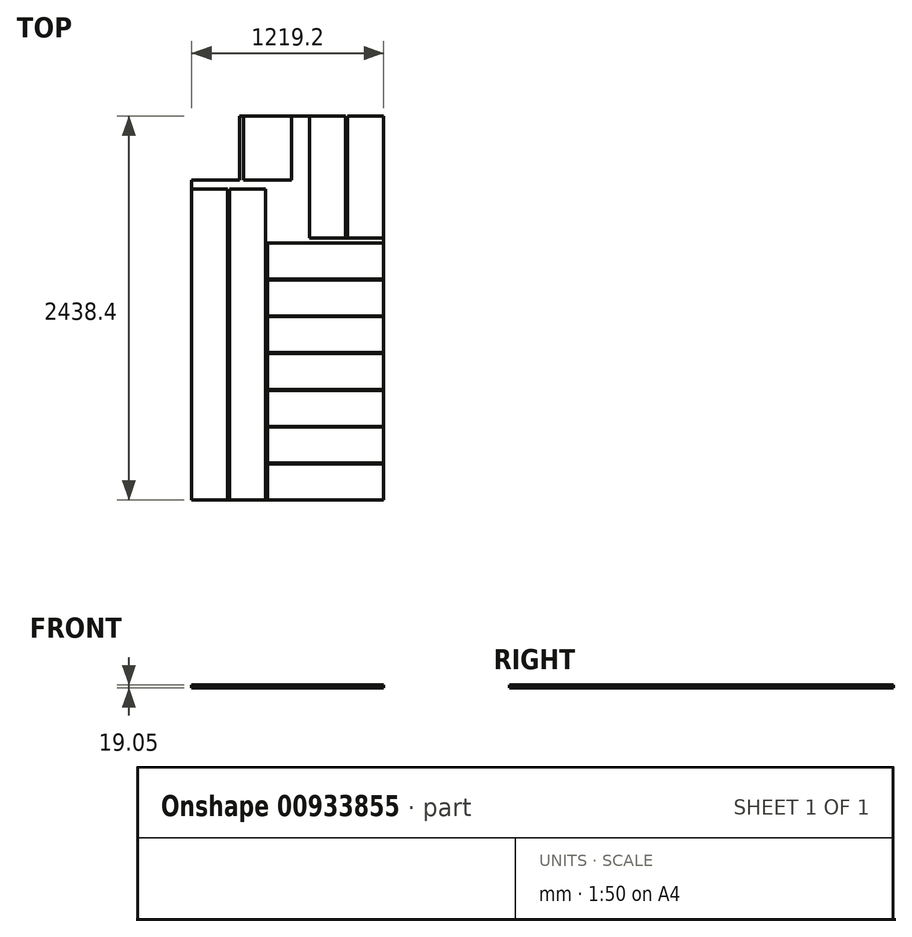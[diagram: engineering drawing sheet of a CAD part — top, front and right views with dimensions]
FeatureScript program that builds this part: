
annotation { "Feature Type Name" : "Feature", "Feature Type Description" : "" }
export const myFeature = defineFeature(function(context is Context, id is Id, definition is map)
    precondition{}
    {
        {
            var Q0;
            Q0=qCreatedBy(makeId("Top.planeOp"),FACE);
            var sketch = newSketch(context, id + "F0", { "sketchPlane" : qUnion([Q0])});
            skLineSegment(sketch, "E0.bottom", {"start": v(0, 0) * mm, "end": v(1219.2, 0) * mm, "construction": true});
            skLineSegment(sketch, "E0.top", {"start": v(0, 2438.4) * mm, "end": v(1219.2, 2438.4) * mm, "construction": true});
            skLineSegment(sketch, "E0.left", {"start": v(0, 0) * mm, "end": v(0, 2438.4) * mm, "construction": true});
            skLineSegment(sketch, "E0.right", {"start": v(1219.2, 0) * mm, "end": v(1219.2, 2438.4) * mm, "construction": true});
            skLineSegment(sketch, "E1.bottom", {"start": v(0, 0) * mm, "end": v(228.6, 0) * mm});
            skLineSegment(sketch, "E1.top", {"start": v(0, 1974.85) * mm, "end": v(228.6, 1974.85) * mm});
            skLineSegment(sketch, "E1.left", {"start": v(0, 0) * mm, "end": v(0, 1974.85) * mm});
            skLineSegment(sketch, "E1.right", {"start": v(228.6, 0) * mm, "end": v(228.6, 1974.85) * mm});
            skLineSegment(sketch, "E2.bottom", {"start": v(241.3, 0) * mm, "end": v(469.9, 0) * mm});
            skLineSegment(sketch, "E2.top", {"start": v(241.3, 1974.85) * mm, "end": v(469.9, 1974.85) * mm});
            skLineSegment(sketch, "E2.left", {"start": v(241.3, 0) * mm, "end": v(241.3, 1974.85) * mm});
            skLineSegment(sketch, "E2.right", {"start": v(469.9, 0) * mm, "end": v(469.9, 1974.85) * mm});
            skLineSegment(sketch, "E3.bottom", {"start": v(1219.2, 0) * mm, "end": v(482.6, 0) * mm});
            skLineSegment(sketch, "E3.top", {"start": v(1219.2, 228.6) * mm, "end": v(482.6, 228.6) * mm});
            skLineSegment(sketch, "E3.left", {"start": v(1219.2, 0) * mm, "end": v(1219.2, 228.6) * mm});
            skLineSegment(sketch, "E3.right", {"start": v(482.6, 0) * mm, "end": v(482.6, 228.6) * mm});
            skLineSegment(sketch, "E4.bottom", {"start": v(1219.2, 233.68) * mm, "end": v(482.6, 233.68) * mm});
            skLineSegment(sketch, "E4.top", {"start": v(1219.2, 462.28) * mm, "end": v(482.6, 462.28) * mm});
            skLineSegment(sketch, "E4.left", {"start": v(1219.2, 233.68) * mm, "end": v(1219.2, 462.28) * mm});
            skLineSegment(sketch, "E4.right", {"start": v(482.6, 233.68) * mm, "end": v(482.6, 462.28) * mm});
            skLineSegment(sketch, "E5.bottom", {"start": v(1219.2, 467.36) * mm, "end": v(482.6, 467.36) * mm});
            skLineSegment(sketch, "E5.top", {"start": v(1219.2, 695.96) * mm, "end": v(482.6, 695.96) * mm});
            skLineSegment(sketch, "E5.left", {"start": v(1219.2, 467.36) * mm, "end": v(1219.2, 695.96) * mm});
            skLineSegment(sketch, "E5.right", {"start": v(482.6, 467.36) * mm, "end": v(482.6, 695.96) * mm});
            skLineSegment(sketch, "E6.bottom", {"start": v(1219.2, 701.04) * mm, "end": v(482.6, 701.04) * mm});
            skLineSegment(sketch, "E6.top", {"start": v(1219.2, 929.64) * mm, "end": v(482.6, 929.64) * mm});
            skLineSegment(sketch, "E6.left", {"start": v(1219.2, 701.04) * mm, "end": v(1219.2, 929.64) * mm});
            skLineSegment(sketch, "E6.right", {"start": v(482.6, 701.04) * mm, "end": v(482.6, 929.64) * mm});
            skLineSegment(sketch, "E7.bottom", {"start": v(1219.2, 934.72) * mm, "end": v(482.6, 934.72) * mm});
            skLineSegment(sketch, "E7.top", {"start": v(1219.2, 1163.32) * mm, "end": v(482.6, 1163.32) * mm});
            skLineSegment(sketch, "E7.left", {"start": v(1219.2, 934.72) * mm, "end": v(1219.2, 1163.32) * mm});
            skLineSegment(sketch, "E7.right", {"start": v(482.6, 934.72) * mm, "end": v(482.6, 1163.32) * mm});
            skLineSegment(sketch, "E8.bottom", {"start": v(1219.2, 1168.4) * mm, "end": v(482.6, 1168.4) * mm});
            skLineSegment(sketch, "E8.top", {"start": v(1219.2, 1397) * mm, "end": v(482.6, 1397) * mm});
            skLineSegment(sketch, "E8.left", {"start": v(1219.2, 1168.4) * mm, "end": v(1219.2, 1397) * mm});
            skLineSegment(sketch, "E8.right", {"start": v(482.6, 1168.4) * mm, "end": v(482.6, 1397) * mm});
            skLineSegment(sketch, "E9.bottom", {"start": v(1219.2, 1402.08) * mm, "end": v(482.6, 1402.08) * mm});
            skLineSegment(sketch, "E9.top", {"start": v(1219.2, 1630.68) * mm, "end": v(482.6, 1630.68) * mm});
            skLineSegment(sketch, "E9.left", {"start": v(1219.2, 1402.08) * mm, "end": v(1219.2, 1630.68) * mm});
            skLineSegment(sketch, "E9.right", {"start": v(482.6, 1402.08) * mm, "end": v(482.6, 1630.68) * mm});
            skLineSegment(sketch, "E10.bottom", {"start": v(1219.2, 2438.4) * mm, "end": v(990.6, 2438.4) * mm});
            skLineSegment(sketch, "E10.top", {"start": v(1219.2, 1663.7) * mm, "end": v(990.6, 1663.7) * mm});
            skLineSegment(sketch, "E10.left", {"start": v(1219.2, 2438.4) * mm, "end": v(1219.2, 1663.7) * mm});
            skLineSegment(sketch, "E10.right", {"start": v(990.6, 2438.4) * mm, "end": v(990.6, 1663.7) * mm});
            skLineSegment(sketch, "E11.bottom", {"start": v(977.9, 2438.4) * mm, "end": v(749.3, 2438.4) * mm});
            skLineSegment(sketch, "E11.top", {"start": v(977.9, 1663.7) * mm, "end": v(749.3, 1663.7) * mm});
            skLineSegment(sketch, "E11.left", {"start": v(977.9, 2438.4) * mm, "end": v(977.9, 1663.7) * mm});
            skLineSegment(sketch, "E11.right", {"start": v(749.3, 2438.4) * mm, "end": v(749.3, 1663.7) * mm});
            skLineSegment(sketch, "E12", {"start": v(749.3, 2438.4) * mm, "end": v(0, 2438.4) * mm});
            skLineSegment(sketch, "E13", {"start": v(0, 1974.85) * mm, "end": v(469.9, 1974.85) * mm});
            skLineSegment(sketch, "E14", {"start": v(0, 2438.4) * mm, "end": v(0, 1974.85) * mm});
            skLineSegment(sketch, "E15", {"start": v(228.6, 1974.85) * mm, "end": v(228.6, 0) * mm});
            skLineSegment(sketch, "E16", {"start": v(228.6, 0) * mm, "end": v(241.3, 0) * mm});
            skLineSegment(sketch, "E17", {"start": v(241.3, 1974.85) * mm, "end": v(241.3, 0) * mm});
            skLineSegment(sketch, "E18", {"start": v(469.9, 1974.85) * mm, "end": v(469.9, 0) * mm});
            skLineSegment(sketch, "E19", {"start": v(469.9, 0) * mm, "end": v(482.6, 0) * mm});
            skLineSegment(sketch, "E20", {"start": v(482.6, 0) * mm, "end": v(482.6, 1630.68) * mm});
            skLineSegment(sketch, "E21", {"start": v(482.6, 1630.68) * mm, "end": v(1219.2, 1630.68) * mm});
            skLineSegment(sketch, "E22", {"start": v(1219.2, 1630.68) * mm, "end": v(1219.2, 1663.7) * mm});
            skLineSegment(sketch, "E23", {"start": v(990.6, 1663.7) * mm, "end": v(990.6, 2438.4) * mm});
            skLineSegment(sketch, "E24", {"start": v(990.6, 2438.4) * mm, "end": v(977.9, 2438.4) * mm});
            skLineSegment(sketch, "E25", {"start": v(990.6, 1663.7) * mm, "end": v(749.3, 1663.7) * mm});
            skLineSegment(sketch, "E26", {"start": v(749.3, 1663.7) * mm, "end": v(749.3, 2438.4) * mm});
            skLineSegment(sketch, "E27", {"start": v(990.6, 1663.7) * mm, "end": v(977.9, 1663.7) * mm});
            skLineSegment(sketch, "E28", {"start": v(1219.2, 228.6) * mm, "end": v(1219.2, 233.68) * mm});
            skLineSegment(sketch, "E29", {"start": v(1219.2, 462.28) * mm, "end": v(1219.2, 467.36) * mm});
            skLineSegment(sketch, "E30", {"start": v(1219.2, 695.96) * mm, "end": v(1219.2, 701.04) * mm});
            skLineSegment(sketch, "E31", {"start": v(1219.2, 929.64) * mm, "end": v(1219.2, 934.72) * mm});
            skLineSegment(sketch, "E32", {"start": v(1219.2, 1163.32) * mm, "end": v(1219.2, 1168.4) * mm});
            skLineSegment(sketch, "E33", {"start": v(1219.2, 1402.08) * mm, "end": v(1219.2, 1397) * mm});
            skLineSegment(sketch, "E34.bottom", {"start": v(0, 2438.4) * mm, "end": v(304.8, 2438.4) * mm});
            skLineSegment(sketch, "E34.top", {"start": v(0, 2032) * mm, "end": v(304.8, 2032) * mm});
            skLineSegment(sketch, "E34.left", {"start": v(0, 2438.4) * mm, "end": v(0, 2032) * mm});
            skLineSegment(sketch, "E34.right", {"start": v(304.8, 2438.4) * mm, "end": v(304.8, 2032) * mm});
            skLineSegment(sketch, "E35.bottom", {"start": v(374.65, 2438.4) * mm, "end": v(679.45, 2438.4) * mm});
            skLineSegment(sketch, "E36.bottom", {"start": v(330.2, 2438.4) * mm, "end": v(635, 2438.4) * mm});
            skLineSegment(sketch, "E36.top", {"start": v(330.2, 2032) * mm, "end": v(635, 2032) * mm});
            skLineSegment(sketch, "E36.left", {"start": v(330.2, 2438.4) * mm, "end": v(330.2, 2032) * mm});
            skLineSegment(sketch, "E36.right", {"start": v(635, 2438.4) * mm, "end": v(635, 2032) * mm});
            skSolve(sketch);
        }
        {
            var Q0;
            Q0=makeQuery(id+"F0.imprint","IMPRINT",FACE,{"disambiguationData":[TD([[makeQuery(id+"F0.imprint","IMPRINT",EDGE,{"derivedFrom":sQuery(id+"F0.wireOp",EDGE,"E12")}),1.0]])]});
            var Q1;
            Q1=makeQuery(id+"F0.imprint","IMPRINT",FACE,{"disambiguationData":[TD([[makeQuery(id+"F0.imprint","IMPRINT",EDGE,{"derivedFrom":sQuery(id+"F0.wireOp",EDGE,"E13")}),-1.0]])]});
            var Q2;
            Q2=makeQuery(id+"F0.imprint","IMPRINT",FACE,{"disambiguationData":[TD([[makeQuery(id+"F0.imprint","IMPRINT",EDGE,{"derivedFrom":sQuery(id+"F0.wireOp",EDGE,"E23")}),1.0]])]});
            var Q3;
            {var subQ0=sQuery(id+"F0.wireOp",EDGE,"E8.top");Q3=makeQuery(id+"F0.imprint","IMPRINT",FACE,{"disambiguationData":[TD([[makeQuery(id+"F0.imprint","IMPRINT",EDGE,{"derivedFrom":subQ0}),-1.0]])]});}
            var Q4;
            {var subQ0=sQuery(id+"F0.wireOp",EDGE,"E7.top");Q4=makeQuery(id+"F0.imprint","IMPRINT",FACE,{"disambiguationData":[TD([[makeQuery(id+"F0.imprint","IMPRINT",EDGE,{"derivedFrom":subQ0}),-1.0]])]});}
            var Q5;
            {var subQ0=sQuery(id+"F0.wireOp",EDGE,"E6.top");Q5=makeQuery(id+"F0.imprint","IMPRINT",FACE,{"disambiguationData":[TD([[makeQuery(id+"F0.imprint","IMPRINT",EDGE,{"derivedFrom":subQ0}),-1.0]])]});}
            var Q6;
            {var subQ0=sQuery(id+"F0.wireOp",EDGE,"E5.top");Q6=makeQuery(id+"F0.imprint","IMPRINT",FACE,{"disambiguationData":[TD([[makeQuery(id+"F0.imprint","IMPRINT",EDGE,{"derivedFrom":subQ0}),-1.0]])]});}
            var Q7;
            {var subQ0=sQuery(id+"F0.wireOp",EDGE,"E4.top");Q7=makeQuery(id+"F0.imprint","IMPRINT",FACE,{"disambiguationData":[TD([[makeQuery(id+"F0.imprint","IMPRINT",EDGE,{"derivedFrom":subQ0}),-1.0]])]});}
            var Q8;
            {var subQ0=sQuery(id+"F0.wireOp",EDGE,"E3.top");Q8=makeQuery(id+"F0.imprint","IMPRINT",FACE,{"disambiguationData":[TD([[makeQuery(id+"F0.imprint","IMPRINT",EDGE,{"derivedFrom":subQ0}),-1.0]])]});}
            extrude(context, id + "F1", {"entities" : qUnion([Q0, Q1, Q2, Q3, Q4, Q5, Q6, Q7, Q8]), "depth" : 19.05 * mm, "offsetDistance" : 25.4 * mm});
        }
        {
            var Q0;
            Q0=makeQuery(id+"F0.imprint","IMPRINT",FACE,{"disambiguationData":[TD([[makeQuery(id+"F0.imprint","IMPRINT",EDGE,{"derivedFrom":sQuery(id+"F0.wireOp",EDGE,"E1.bottom")}),1.0]])]});
            var Q1;
            Q1=makeQuery(id+"F0.imprint","IMPRINT",FACE,{"disambiguationData":[TD([[makeQuery(id+"F0.imprint","IMPRINT",EDGE,{"derivedFrom":sQuery(id+"F0.wireOp",EDGE,"E2.bottom")}),1.0]])]});
            var Q2;
            {var subQ0=sQuery(id+"F0.wireOp",EDGE,"E9.bottom");Q2=makeQuery(id+"F0.imprint","IMPRINT",FACE,{"disambiguationData":[TD([[makeQuery(id+"F0.imprint","IMPRINT",EDGE,{"derivedFrom":subQ0}),-1.0]])]});}
            var Q3;
            {var subQ0=sQuery(id+"F0.wireOp",EDGE,"E8.bottom");Q3=makeQuery(id+"F0.imprint","IMPRINT",FACE,{"disambiguationData":[TD([[makeQuery(id+"F0.imprint","IMPRINT",EDGE,{"derivedFrom":subQ0}),-1.0]])]});}
            var Q4;
            {var subQ0=sQuery(id+"F0.wireOp",EDGE,"E7.bottom");Q4=makeQuery(id+"F0.imprint","IMPRINT",FACE,{"disambiguationData":[TD([[makeQuery(id+"F0.imprint","IMPRINT",EDGE,{"derivedFrom":subQ0}),-1.0]])]});}
            var Q5;
            {var subQ0=sQuery(id+"F0.wireOp",EDGE,"E6.bottom");Q5=makeQuery(id+"F0.imprint","IMPRINT",FACE,{"disambiguationData":[TD([[makeQuery(id+"F0.imprint","IMPRINT",EDGE,{"derivedFrom":subQ0}),-1.0]])]});}
            var Q6;
            {var subQ0=sQuery(id+"F0.wireOp",EDGE,"E5.bottom");Q6=makeQuery(id+"F0.imprint","IMPRINT",FACE,{"disambiguationData":[TD([[makeQuery(id+"F0.imprint","IMPRINT",EDGE,{"derivedFrom":subQ0}),-1.0]])]});}
            var Q7;
            {var subQ0=sQuery(id+"F0.wireOp",EDGE,"E4.bottom");Q7=makeQuery(id+"F0.imprint","IMPRINT",FACE,{"disambiguationData":[TD([[makeQuery(id+"F0.imprint","IMPRINT",EDGE,{"derivedFrom":subQ0}),-1.0]])]});}
            var Q8;
            {var subQ0=sQuery(id+"F0.wireOp",EDGE,"E3.bottom");Q8=makeQuery(id+"F0.imprint","IMPRINT",FACE,{"disambiguationData":[TD([[makeQuery(id+"F0.imprint","IMPRINT",EDGE,{"derivedFrom":subQ0}),-1.0]])]});}
            var Q9;
            Q9=makeQuery(id+"F0.imprint","IMPRINT",FACE,{"disambiguationData":[TD([[makeQuery(id+"F0.imprint","IMPRINT",EDGE,{"derivedFrom":sQuery(id+"F0.wireOp",EDGE,"E11.bottom")}),1.0]])]});
            var Q10;
            Q10=makeQuery(id+"F0.imprint","IMPRINT",FACE,{"disambiguationData":[TD([[makeQuery(id+"F0.imprint","IMPRINT",EDGE,{"derivedFrom":sQuery(id+"F0.wireOp",EDGE,"E10.bottom")}),1.0]])]});
            var Q11;
            Q11=makeQuery(id+"F0.imprint","IMPRINT",FACE,{"disambiguationData":[TD([[makeQuery(id+"F0.imprint","IMPRINT",EDGE,{"derivedFrom":sQuery(id+"F0.wireOp",EDGE,"E34.bottom")}),-1.0]])]});
            var Q12;
            Q12=makeQuery(id+"F0.imprint","IMPRINT",FACE,{"disambiguationData":[TD([[makeQuery(id+"F0.imprint","IMPRINT",EDGE,{"derivedFrom":sQuery(id+"F0.wireOp",EDGE,"E36.top")}),1.0]])]});
            extrude(context, id + "F2", {"entities" : qUnion([Q0, Q1, Q2, Q3, Q4, Q5, Q6, Q7, Q8, Q9, Q10, Q11, Q12]), "depth" : 19.05 * mm, "offsetDistance" : 25.4 * mm});
        }
    });
